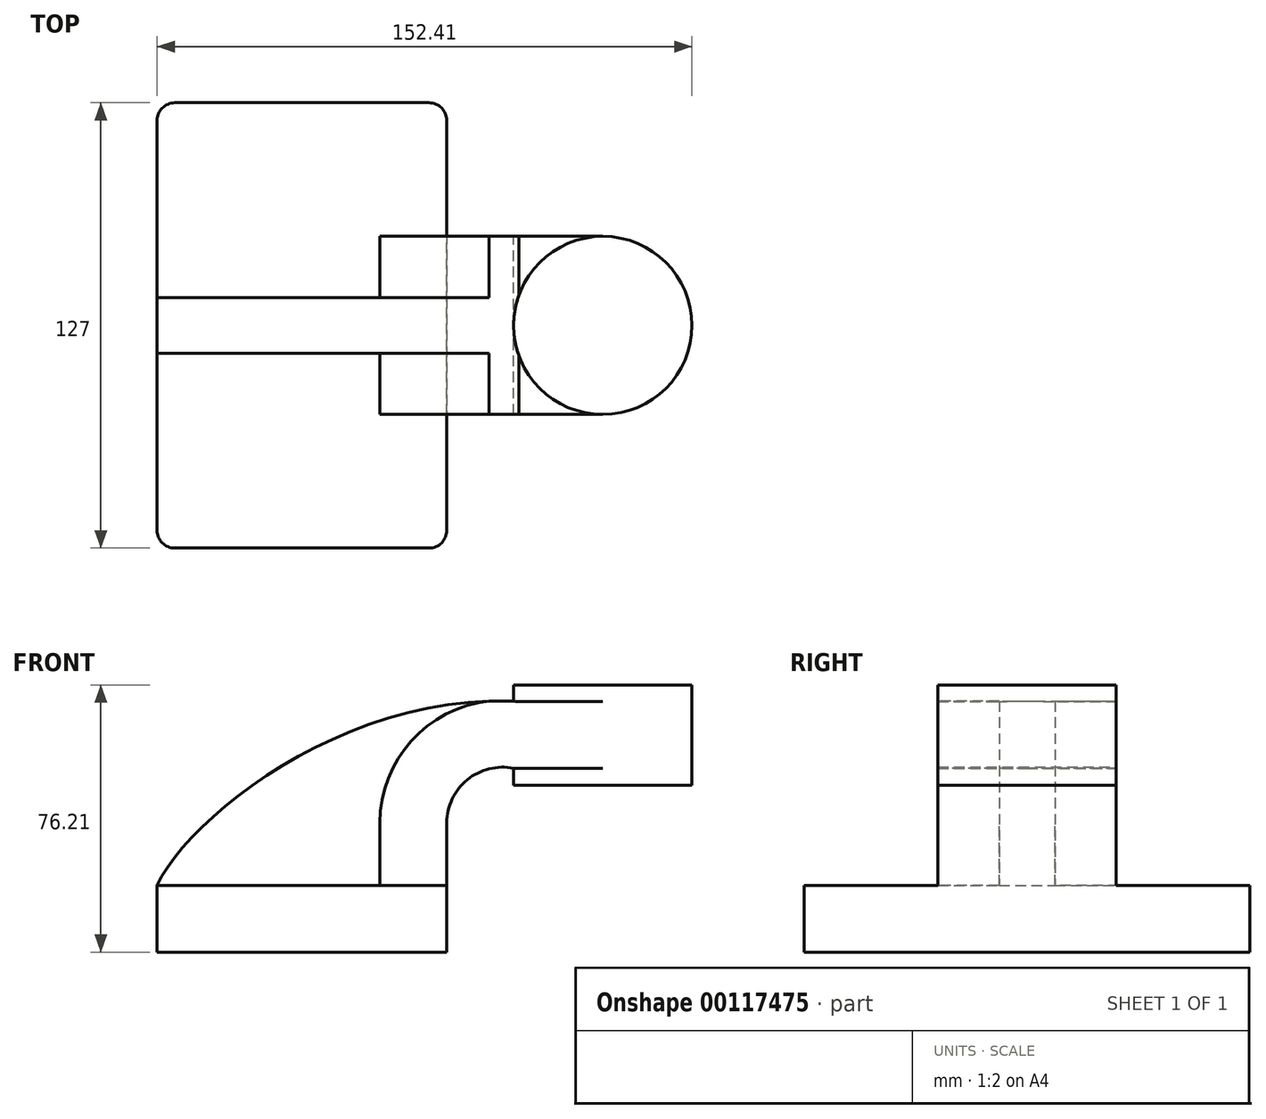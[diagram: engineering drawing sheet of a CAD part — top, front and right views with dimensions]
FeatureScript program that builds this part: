
annotation { "Feature Type Name" : "Feature", "Feature Type Description" : "" }
export const myFeature = defineFeature(function(context is Context, id is Id, definition is map)
    precondition{}
    {
        {
            var Q0;
            Q0=qCreatedBy(makeId("Front.planeOp"),FACE);
            var sketch = newSketch(context, id + "F0", { "sketchPlane" : qUnion([Q0])});
            skLineSegment(sketch, "E0.bottom", {"start": v(-41.28, -9.52) * mm, "end": v(41.28, -9.52) * mm});
            skLineSegment(sketch, "E0.top", {"start": v(-41.28, 9.53) * mm, "end": v(41.28, 9.53) * mm});
            skLineSegment(sketch, "E0.left", {"start": v(-41.28, -9.52) * mm, "end": v(-41.28, 9.53) * mm});
            skLineSegment(sketch, "E0.right", {"start": v(41.28, -9.53) * mm, "end": v(41.28, 9.53) * mm});
            skPoint(sketch, "E0.middle", {"position": v(0, 0) * mm});
            skLineSegment(sketch, "E1.bottom", {"start": v(111.13, 38.1) * mm, "end": v(60.33, 38.1) * mm});
            skLineSegment(sketch, "E1.top", {"start": v(111.13, 66.68) * mm, "end": v(60.33, 66.68) * mm});
            skLineSegment(sketch, "E1.left", {"start": v(111.13, 38.1) * mm, "end": v(111.13, 66.68) * mm});
            skLineSegment(sketch, "E1.right", {"start": v(60.33, 38.1) * mm, "end": v(60.33, 66.68) * mm});
            skPoint(sketch, "E1.middle", {"position": v(85.72, 52.39) * mm});
            skLineSegment(sketch, "E2", {"start": v(41.28, 9.53) * mm, "end": v(41.28, 27.32) * mm});
            skArc(sketch, "E3", {"start": v(41.27, 27.32) * mm, "mid": v(47.1, 39.62) * mm, "end": v(60.33, 42.88) * mm});
            skLineSegment(sketch, "E4", {"start": v(60.33, 42.88) * mm, "end": v(85.72, 42.88) * mm});
            skLineSegment(sketch, "E5.0", {"start": v(61.87, 61.93) * mm, "end": v(85.72, 61.93) * mm});
            skArc(sketch, "E5.1", {"start": v(22.22, 27.32) * mm, "mid": v(34.18, 53.63) * mm, "end": v(61.87, 61.93) * mm});
            skLineSegment(sketch, "E5.2", {"start": v(22.22, 9.53) * mm, "end": v(22.22, 27.32) * mm});
            skLineSegment(sketch, "E6", {"start": v(85.73, 38.1) * mm, "end": v(85.73, 66.68) * mm});
            skFitSpline(sketch, "E7", {"points": [v(61.87, 61.93) * mm, v(-41.28, 9.53) * mm], "startDerivative": vector(-147.34, 8.47) * mm, "endDerivative": vector(-27.51, -58.93) * mm});
            skSolve(sketch);
        }
        {
            var Q0;
            Q0=makeQuery(id+"F0.imprint","IMPRINT",FACE,{"disambiguationData":[TD([[makeQuery(id+"F0.imprint","IMPRINT",EDGE,{"derivedFrom":sQuery(id+"F0.wireOp",EDGE,"E0.bottom")}),1.0]])]});
            extrude(context, id + "F1", {"entities" : qUnion([Q0]), "endBound" : BoundingType.SYMMETRIC, "oppositeDirection" : true, "depth" : 127 * mm});
        }
        {
            var Q0;
            {var subQ6=sQuery(id+"F0.wireOp",EDGE,"E2");Q0=makeQuery(id+"F0.imprint","IMPRINT",FACE,{"disambiguationData":[TD([[makeQuery(id+"F0.imprint","IMPRINT",EDGE,{"derivedFrom":subQ6}),1.0]])]});}
            extrude(context, id + "F2", {"entities" : qUnion([Q0]), "operationType" : NewBodyOperationType.ADD, "endBound" : BoundingType.SYMMETRIC, "depth" : 50.8 * mm});
        }
        {
            var Q0;
            {var subQ1=sQuery(id+"F0.wireOp",EDGE,"E4");Q0=makeQuery(id+"F0.imprint","IMPRINT",FACE,{"disambiguationData":[TD([[makeQuery(id+"F0.imprint","IMPRINT",EDGE,{"derivedFrom":subQ1}),1.0]])]});}
            extrude(context, id + "F3", {"entities" : qUnion([Q0]), "operationType" : NewBodyOperationType.ADD, "endBound" : BoundingType.SYMMETRIC, "depth" : 50.8 * mm});
        }
        {
            var Q0;
            {var subQ3=sQuery(id+"F0.wireOp",EDGE,"E5.2");Q0=makeQuery(id+"F0.imprint","IMPRINT",FACE,{"disambiguationData":[TD([[makeQuery(id+"F0.imprint","IMPRINT",EDGE,{"derivedFrom":subQ3}),1.0]])]});}
            extrude(context, id + "F4", {"entities" : qUnion([Q0]), "operationType" : NewBodyOperationType.ADD, "endBound" : BoundingType.SYMMETRIC, "depth" : 15.88 * mm});
        }
        {
            var Q0;
            {var subQ0=sQuery(id+"F0.wireOp",EDGE,"E1.left");Q0=makeQuery(id+"F0.imprint","IMPRINT",FACE,{"disambiguationData":[TD([[makeQuery(id+"F0.imprint","IMPRINT",EDGE,{"derivedFrom":subQ0}),1.0]])]});}
            var Q1;
            Q1=sQuery(id+"F0.wireOp",EDGE,"E6");
            revolve(context, id + "F5", {"operationType" : NewBodyOperationType.ADD, "entities" : qUnion([Q0]), "axis" : qUnion([Q1]), "revolveType" : RevolveType.FULL});
        }
        {
            var Q0;
            Q0=makeQuery(id+"F1.opExtrude","CAP_EDGE",EDGE,{"disambiguationData":[OSD([sQuery(id+"F0.wireOp",EDGE,"E0.left")])],"isStart":true});
            var Q1;
            Q1=makeQuery(id+"F1.opExtrude","CAP_EDGE",EDGE,{"disambiguationData":[OSD([sQuery(id+"F0.wireOp",EDGE,"E0.right")])],"isStart":true});
            var Q2;
            Q2=makeQuery(id+"F1.opExtrude","CAP_EDGE",EDGE,{"disambiguationData":[OSD([sQuery(id+"F0.wireOp",EDGE,"E0.left")])],"isStart":false});
            fillet(context, id + "F6", {"entities" : qUnion([Q0, Q1, Q2]), "radius" : 5.08 * mm, "tangentPropagation" : true, "allowEdgeOverflow" : false});
        }
        {
            var Q0;
            Q0=makeQuery(id+"F1.opExtrude","CAP_EDGE",EDGE,{"disambiguationData":[OSD([sQuery(id+"F0.wireOp",EDGE,"E0.right")])],"isStart":false});
            fillet(context, id + "F7", {"entities" : qUnion([Q0]), "radius" : 5.08 * mm, "tangentPropagation" : true, "allowEdgeOverflow" : false});
        }
    });
